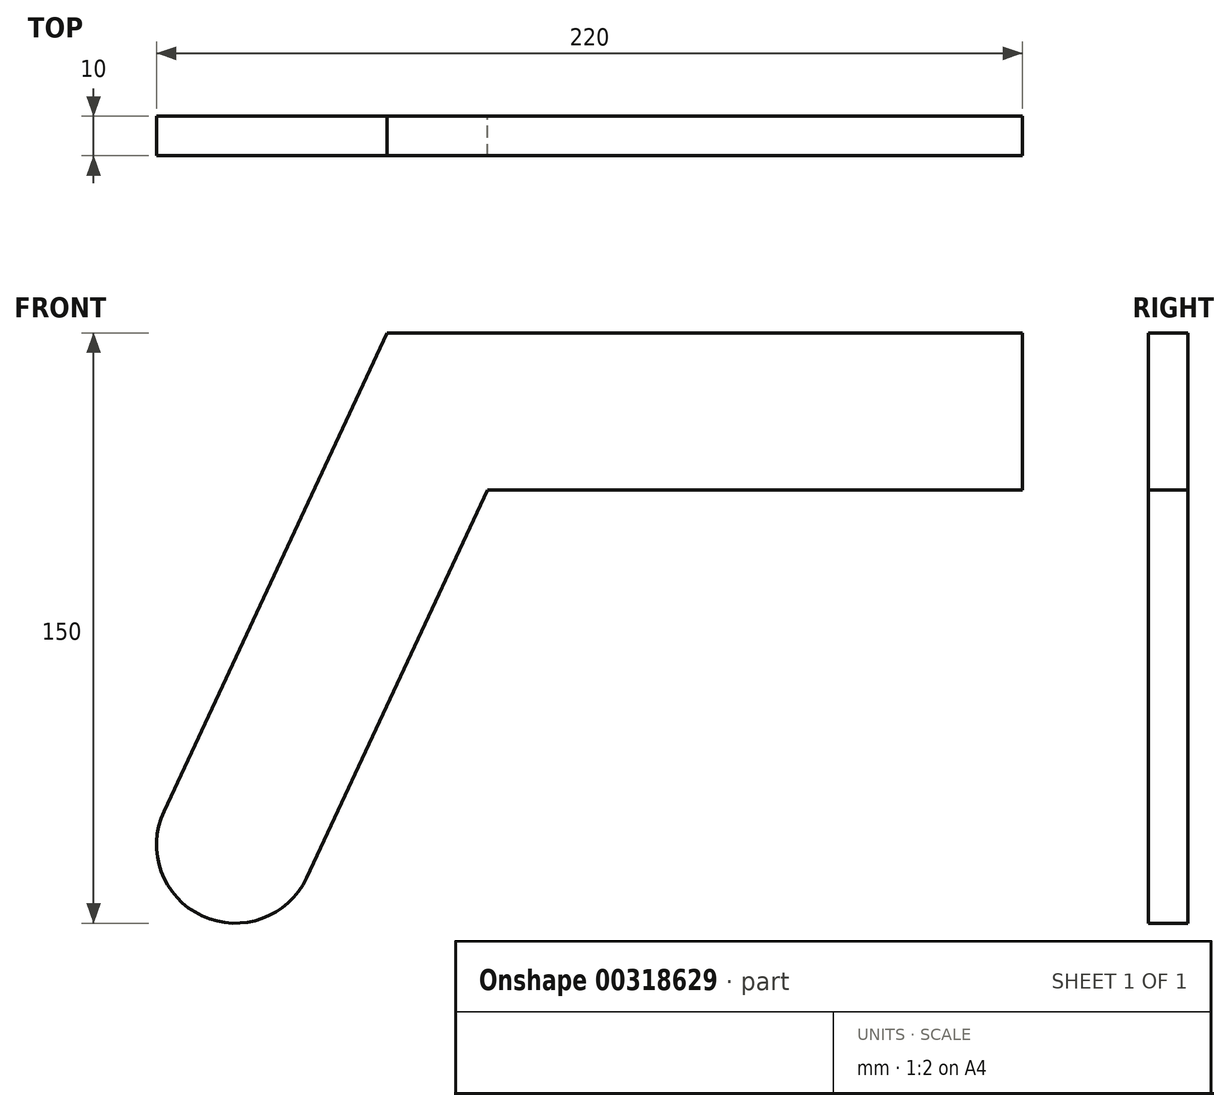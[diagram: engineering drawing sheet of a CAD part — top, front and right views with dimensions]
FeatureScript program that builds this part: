
annotation { "Feature Type Name" : "Feature", "Feature Type Description" : "" }
export const myFeature = defineFeature(function(context is Context, id is Id, definition is map)
    precondition{}
    {
        {
            var Q0;
            Q0=qCreatedBy(makeId("Front.planeOp"),FACE);
            var sketch = newSketch(context, id + "F0", { "sketchPlane" : qUnion([Q0])});
            skLineSegment(sketch, "E0", {"start": v(-18.13, 8.45) * mm, "end": v(38.55, 130) * mm});
            skLineSegment(sketch, "E1", {"start": v(38.55, 130) * mm, "end": v(200, 130) * mm});
            skLineSegment(sketch, "E2", {"start": v(200, 130) * mm, "end": v(200, 90) * mm});
            skLineSegment(sketch, "E3", {"start": v(200, 90) * mm, "end": v(64.04, 90) * mm});
            skLineSegment(sketch, "E4", {"start": v(64.04, 90) * mm, "end": v(18.13, -8.45) * mm});
            skArc(sketch, "E5", {"start": v(-18.13, 8.45) * mm, "mid": v(-8.45, -18.13) * mm, "end": v(18.13, -8.45) * mm});
            skSolve(sketch);
        }
        {
            var Q0;
            Q0=makeQuery(id+"F0.imprint","IMPRINT",FACE,{"disambiguationData":[TD([[makeQuery(id+"F0.imprint","IMPRINT",EDGE,{"derivedFrom":sQuery(id+"F0.wireOp",EDGE,"E0")}),-1.0]])]});
            extrude(context, id + "F1", {"entities" : qUnion([Q0]), "depth" : 10 * mm});
        }
    });
